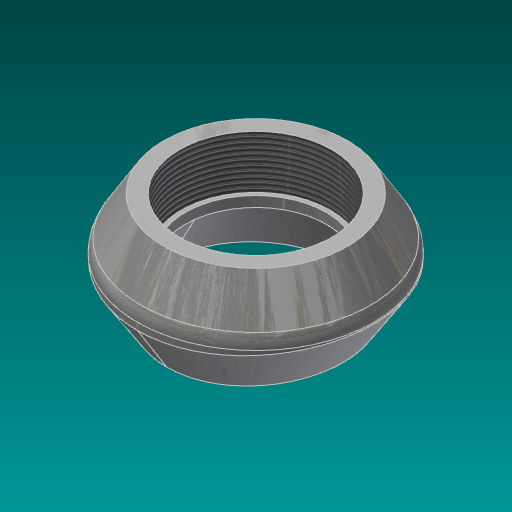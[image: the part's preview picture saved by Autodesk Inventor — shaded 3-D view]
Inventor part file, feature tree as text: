
AUTODESK INVENTOR PART (.ipt)
format: ipt  version: 2017.3 (Build 213256000, 256)  size: 449,024 bytes
history: native  units: mm (DEFAULTED — no unit token found)
features: other x8, sketch x5, plane x1, extrude x1, revolve x1, thread x1, sweep x1
ambient origin geometry x8: Origin, YZ Plane, XZ Plane, XY Plane, X Axis, Y Axis, Z Axis, Center Point
bodies: Solid1 (feature_tree)
feature tree (18):
  sketch  "Sketch1"  dims[d5=38.1mm d8=90.0deg]
  plane  "Work Plane1"
  sketch  "Sketch2"  dims[d9=0.0mm d10=847.725mm d11=10.0mm d12=0.0mm]
  extrude  "Extrusion1"  TaperAngle=90.0deg  [1 undecoded]
  revolve  "Revolution2"  [1 undecoded]
  thread  "Thread1"  [1 undecoded]
  other  "Work Point1"
  sweep  "Sweep1"
  other  "Work Axis3"
  other  "Work Point2"
  other  "Work Point3"
  sketch  "Sketch3"  dims[d45=8.810625mm d52=88.10625mm]
  sketch  "Sketch4"  dims[d54=1097.75625mm d77=68.1482mm d80=38.1mm d81=19.2151mm d83=56.55818mm d85=0.312398mm d86=90.0deg d91=52.5018mm d92=6.0mm d93=4.0mm d94=2.0mm d95=90.0deg d96=3.84302mm d97=0.0mm d102=10.0mm d103=0.0mm d106=19.05mm d107=461.9625mm d120=-423.8625mm d121=0.0mm d129=0.78232mm d130=0.78232mm d131=30.0deg d132=11.509375mm d133=0.0mm d134=0.0mm d135=90.0deg d136=0.0mm d137=90.0deg d138=65.0875mm d139=58.3692mm d140=0.0mm]
  other  "Work Axis2"
  sketch  "3D Sketch1"
  other  "Edges14"
  other  "Edges15"
  other  "Work Axis4"
note: 3 required parameter values undecoded (feature->parameter linkage not recoverable at this tier; creation-order binding heuristic only, values carry confidence <= 0.55)